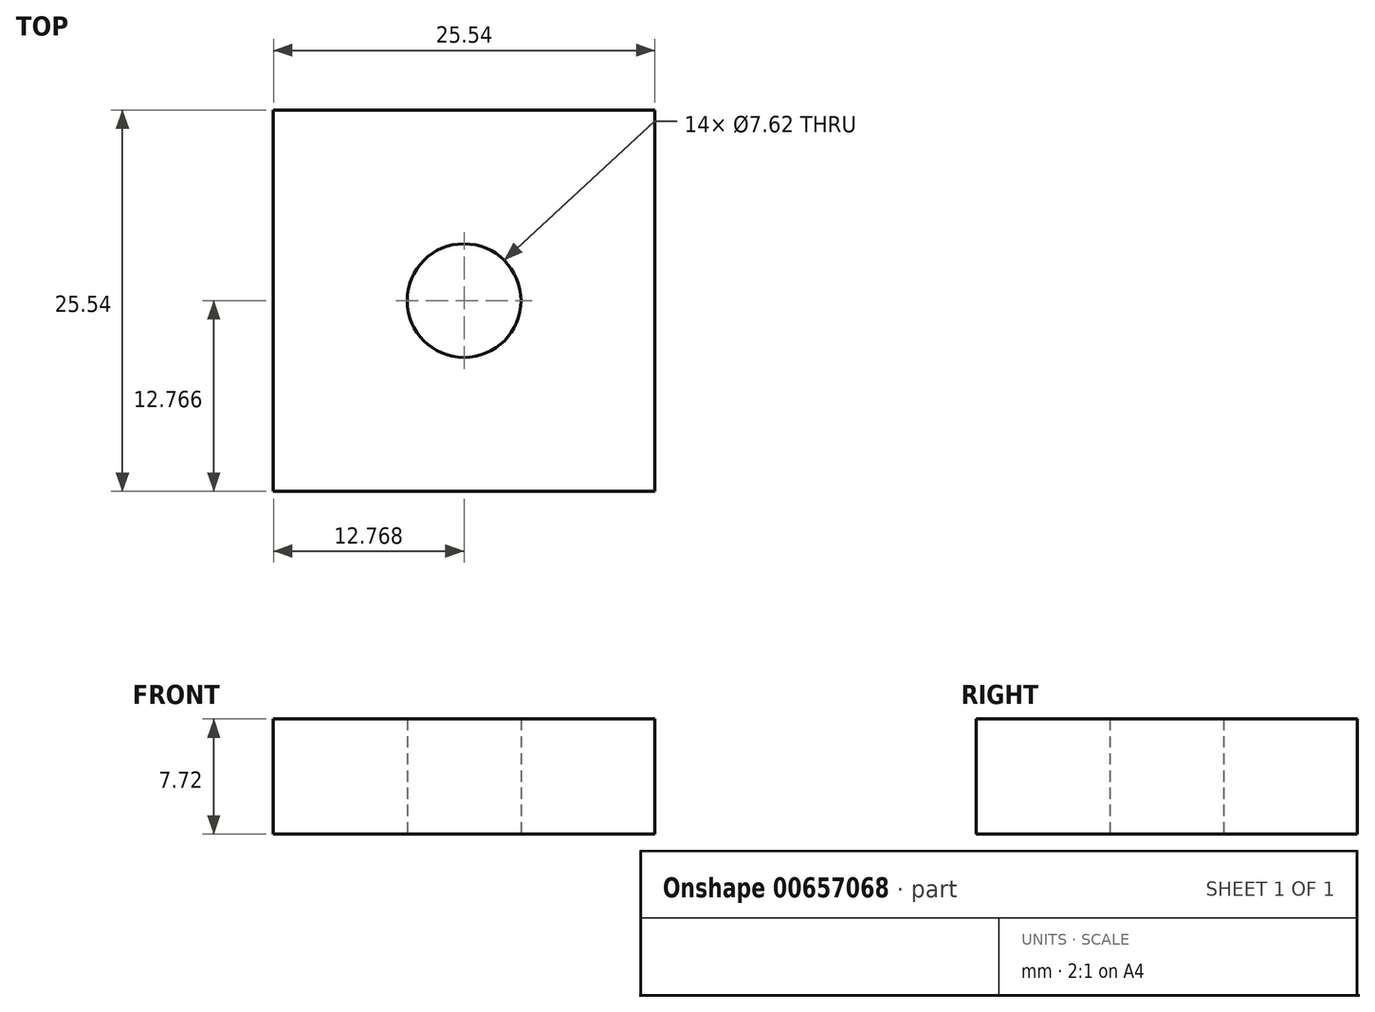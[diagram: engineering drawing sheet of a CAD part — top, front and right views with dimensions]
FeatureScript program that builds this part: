
annotation { "Feature Type Name" : "Feature", "Feature Type Description" : "" }
export const myFeature = defineFeature(function(context is Context, id is Id, definition is map)
    precondition{}
    {
        {
            var Q0;
            Q0=qCreatedBy(makeId("Top.planeOp"),FACE);
            var sketch = newSketch(context, id + "F0", { "sketchPlane" : qUnion([Q0])});
            skCircle(sketch, "E0", {"center": v(-2.8, -0.43) * mm, "radius": 3.81 * mm});
            skLineSegment(sketch, "E1.bottom", {"start": v(9.98, -13.2) * mm, "end": v(-15.56, -13.2) * mm});
            skLineSegment(sketch, "E1.top", {"start": v(9.98, 12.34) * mm, "end": v(-15.56, 12.34) * mm});
            skLineSegment(sketch, "E1.left", {"start": v(9.98, -13.2) * mm, "end": v(9.98, 12.34) * mm});
            skLineSegment(sketch, "E1.right", {"start": v(-15.56, -13.2) * mm, "end": v(-15.56, 12.34) * mm});
            skSolve(sketch);
        }
        {
            var Q0;
            Q0 = qSketchRegion(id + "F0", true);
            extrude(context, id + "F1", {"entities" : qUnion([Q0]), "depth" : 7.02 * mm, "offsetDistance" : 25 * mm, "hasSecondDirection" : true, "secondDirectionOppositeDirection" : true, "secondDirectionDepth" : .7 * mm});
        }
    });
